# Revit family: GEK_Конвектор_ECO_Внутрипольный_ПроходногоТипа_GEKON
name_source: partatom
category: Оборудование
units: mm (PartAtom-declared; Revit-internal decimal feet)

## family parameters
Всегда вертикально = Нет
Классификация = Нет
На основе рабочей плоскости = Нет
Общий = Нет
При загрузке вырезать с полостями = Нет
Размер круглого соединителя = Использовать диаметр
Тип детали = Нормальный
Точка расчета площади = Нет

## types (12) — shared parameters
ADSK_URL документации изделия = https://gekon.pro
ADSK_URL страницы изделия = https://gekon.pro
ADSK_Версия Revit = 2019
ADSK_Единица измерения = шт.
ADSK_Завод-изготовитель = ООО «Гекон»
ADSK_Количество = 1
ADSK_Обозначение = ГОСТ 31311-2005
ADSK_Размер_Диаметр = 15 мм
BL_BIM library = https://bimlib.pro
URL = https://gekon.pro
Вид профиля решетки_UBL = ● : UBL
Вид профиля решетки_UBR = ● : UBR
Вид профиля решетки_UDB = ● : UDB
Вид профиля решетки_ULB = ● : ULB
Вид профиля решетки_UNA = ● : UNA
Диаметр заглушек = 40 мм
Изготовитель = ООО «Гекон»
Испытательное давление = 24 атм
Максимальная температура теплоносителя = 110 °C
Материал корпуса = GEK_Серый_Корпус_GEKON
Описание = Конвекторы Gekon Eco и Gekon Vent – это канальный прибор отопления с естественной (модель Eco) и принудительной (модель Vent) конвекцией для монтажа в конструкции пола.
Рабочее давление = 16 атм

## per-type parameters (varying)
| type | ADSK_Размер_Высота | ADSK_Размер_Глубина | Заглушки_Справа_Y1 | Заглушки_Справа_Y2 | Заглушки_Справа_Y3 | Заглушки_Справа_Y4 |
| H=8 см, B=18 см | 80 мм | 180 мм | 70 мм | 55 мм | 99 мм | 1 мм |
| H=9 см, B=18 см | 90 мм | 180 мм | 70 мм | 55 мм | 99 мм | 1 мм |
| H=11 см, B=18 см | 110 мм | 180 мм | 70 мм | 55 мм | 99 мм | 1 мм |
| H=8 см, B=23 см | 80 мм | 230 мм | 40 мм | 40 мм | 40 мм | 155 мм |
| H=9 см, B=23 см | 90 мм | 230 мм | 40 мм | 40 мм | 40 мм | 155 мм |
| H=11 см, B=23 см | 110 мм | 230 мм | 40 мм | 40 мм | 40 мм | 155 мм |
| H=8 см, B=30 см | 80 мм | 300 мм | 40 мм | 60 мм | 40 мм | 180 мм |
| H=9 см, B=30 см | 90 мм | 300 мм | 40 мм | 60 мм | 40 мм | 180 мм |
| H=11 см, B=30 см | 110 мм | 300 мм | 40 мм | 60 мм | 40 мм | 180 мм |
| H=8 см, B=38 см | 80 мм | 380 мм | 40 мм | 90 мм | 40 мм | 205 мм |
| H=9 см, B=38 см | 90 мм | 380 мм | 40 мм | 90 мм | 40 мм | 205 мм |
| H=11 см, B=38 см | 110 мм | 380 мм | 40 мм | 90 мм | 40 мм | 205 мм |
